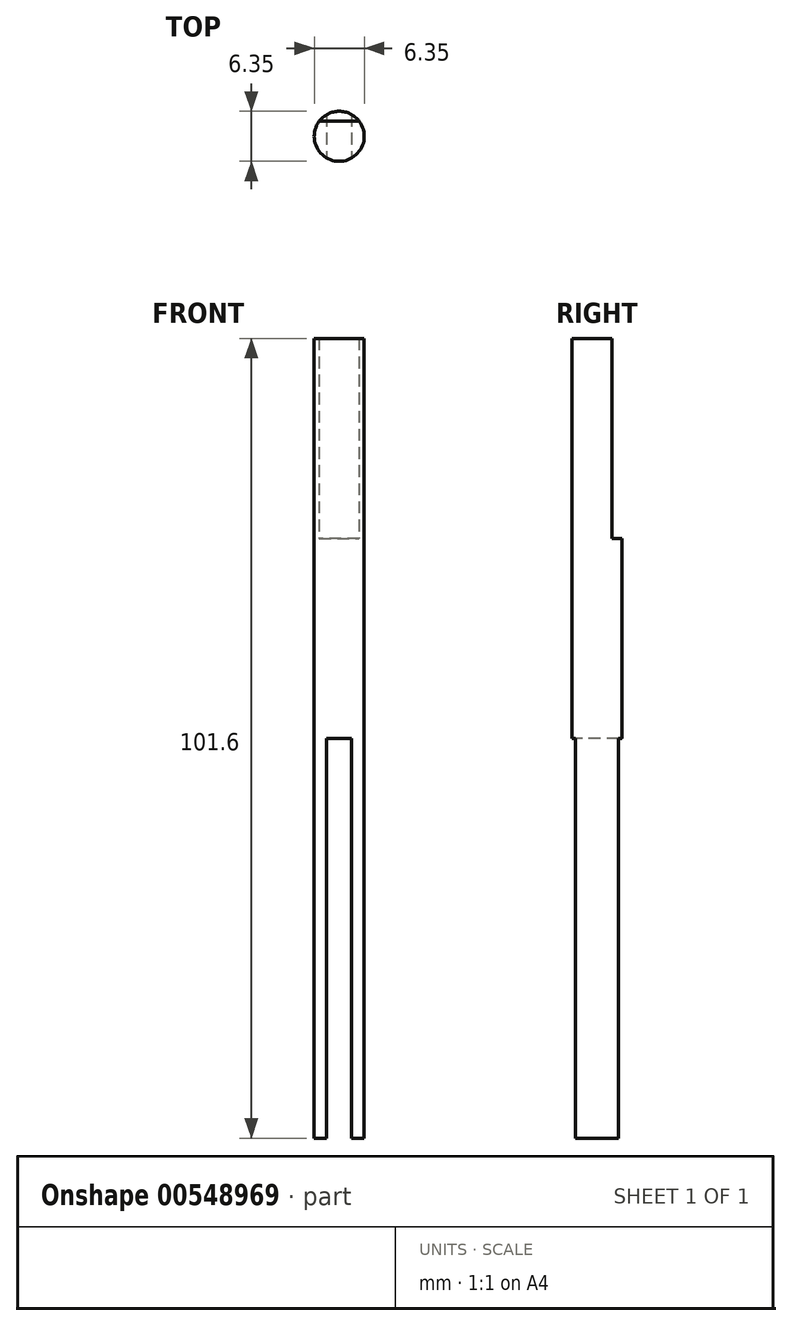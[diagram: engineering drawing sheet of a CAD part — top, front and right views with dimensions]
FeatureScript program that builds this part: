
annotation { "Feature Type Name" : "Feature", "Feature Type Description" : "" }
export const myFeature = defineFeature(function(context is Context, id is Id, definition is map)
    precondition{}
    {
        {
            var Q0;
            Q0=qCreatedBy(makeId("Top.planeOp"),FACE);
            var sketch = newSketch(context, id + "F0", { "sketchPlane" : qUnion([Q0])});
            skCircle(sketch, "E0", {"center": v(-45.72, 18.5) * mm, "radius": 3.18 * mm});
            skSolve(sketch);
        }
        {
            var Q0;
            Q0=makeQuery(id+"F0.imprint","IMPRINT",FACE,{"disambiguationData":[TD([[makeQuery(id+"F0.imprint","IMPRINT",EDGE,{"derivedFrom":sQuery(id+"F0.wireOp",EDGE,"E0")}),1.0]])]});
            extrude(context, id + "F1", {"entities" : qUnion([Q0]), "depth" : 76.2 * mm, "offsetDistance" : 25.4 * mm});
        }
        {
            var Q0;
            Q0=makeQuery(id+"F1.opExtrude","CAP_FACE",FACE,{"disambiguationData":[OSD([sQuery(id+"F0.wireOp",EDGE,"E0")])],"isStart":false});
            var sketch = newSketch(context, id + "F2", { "sketchPlane" : qUnion([Q0])});
            skArc(sketch, "E1", {"start": v(-48.26, 20.41) * mm, "mid": v(-45.72, 15.33) * mm, "end": v(-43.18, 20.41) * mm});
            skLineSegment(sketch, "E2", {"start": v(-48.26, 20.41) * mm, "end": v(-43.18, 20.41) * mm});
            skSolve(sketch);
        }
        {
            var Q0;
            Q0=makeQuery(id+"F2.imprint","IMPRINT",FACE,{"disambiguationData":[TD([[makeQuery(id+"F2.imprint","IMPRINT",EDGE,{"derivedFrom":sQuery(id+"F2.wireOp",EDGE,"E1")}),1.0]])]});
            extrude(context, id + "F3", {"entities" : qUnion([Q0]), "operationType" : NewBodyOperationType.ADD, "depth" : 25.4 * mm, "offsetDistance" : 25.4 * mm});
        }
        {
            var Q0;
            Q0=makeQuery(id+"F1.opExtrude","CAP_FACE",FACE,{"disambiguationData":[OSD([sQuery(id+"F0.wireOp",EDGE,"E0")])],"isStart":true});
            var sketch = newSketch(context, id + "F4", { "sketchPlane" : qUnion([Q0])});
            skLineSegment(sketch, "E3", {"start": v(-47.3, -21.26) * mm, "end": v(-47.3, -15.76) * mm});
            skLineSegment(sketch, "E4", {"start": v(-44.13, -21.26) * mm, "end": v(-44.13, -15.76) * mm});
            skCircle(sketch, "E5", {"center": v(-45.72, -18.5) * mm, "radius": 3.18 * mm});
            skSolve(sketch);
        }
        {
            var Q0;
            {var subQ0=sQuery(id+"F4.wireOp",EDGE,"E3");Q0=makeQuery(id+"F4.imprint","IMPRINT",FACE,{"disambiguationData":[TD([[makeQuery(id+"F4.imprint","IMPRINT",EDGE,{"derivedFrom":subQ0}),-1.0]])]});}
            extrude(context, id + "F5", {"entities" : qUnion([Q0]), "operationType" : NewBodyOperationType.REMOVE, "oppositeDirection" : true, "depth" : 50.8 * mm, "offsetDistance" : 25.4 * mm});
        }
    });
